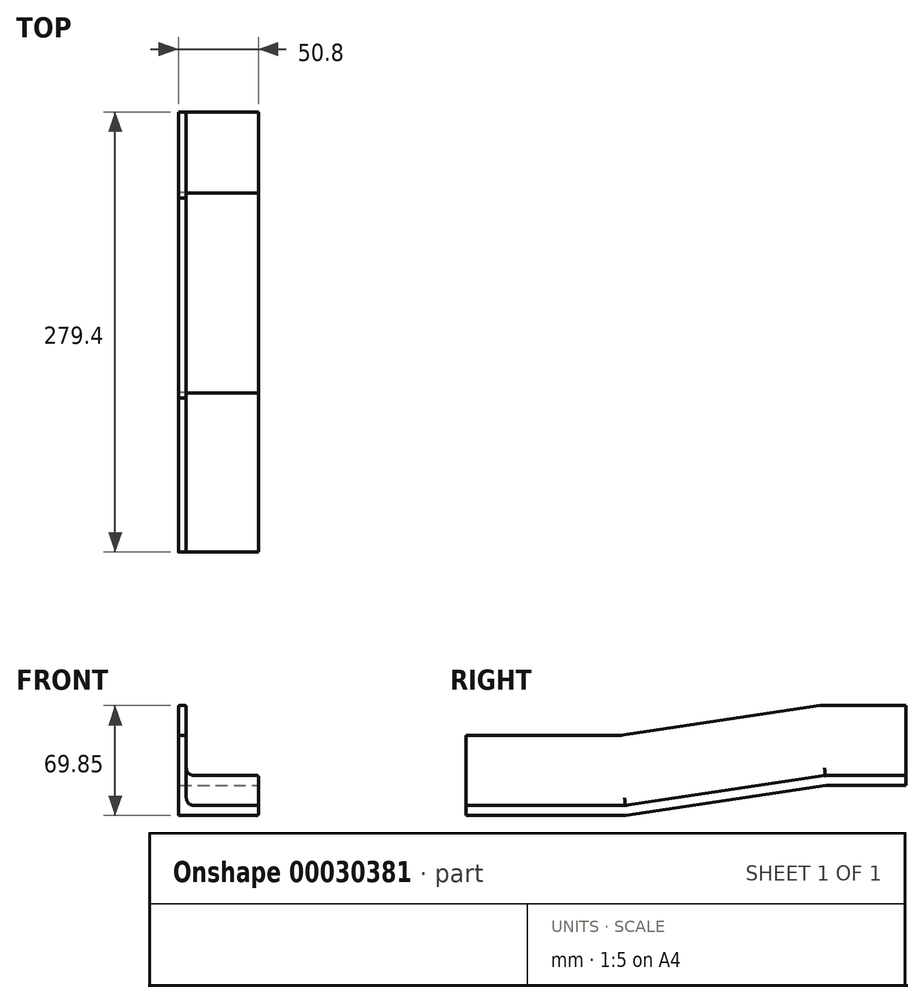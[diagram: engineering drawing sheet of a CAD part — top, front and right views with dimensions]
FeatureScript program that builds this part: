
annotation { "Feature Type Name" : "Feature", "Feature Type Description" : "" }
export const myFeature = defineFeature(function(context is Context, id is Id, definition is map)
    precondition{}
    {
        {
            var Q0;
            Q0=qCreatedBy(makeId("Front.planeOp"),FACE);
            var sketch = newSketch(context, id + "F0", { "sketchPlane" : qUnion([Q0])});
            skLineSegment(sketch, "E0", {"start": v(0, 50.01) * mm, "end": v(0, 0.79) * mm});
            skLineSegment(sketch, "E1", {"start": v(0.79, 0) * mm, "end": v(50.01, 0) * mm});
            skLineSegment(sketch, "E2", {"start": v(50.8, 0.79) * mm, "end": v(50.8, 5.56) * mm});
            skLineSegment(sketch, "E3", {"start": v(50.01, 6.35) * mm, "end": v(9.9, 6.35) * mm});
            skLineSegment(sketch, "E4", {"start": v(5.08, 11.18) * mm, "end": v(5.08, 50.01) * mm});
            skLineSegment(sketch, "E5", {"start": v(4.3, 50.8) * mm, "end": v(0.79, 50.8) * mm});
            skArc(sketch, "E6.filletArc", {"start": v(5.08, 11.18) * mm, "mid": v(6.5, 7.76) * mm, "end": v(9.9, 6.35) * mm});
            skPoint(sketch, "E7.visualSharp", {"position": v(0, 50.8) * mm});
            skArc(sketch, "E7.filletArc", {"start": v(0.79, 50.8) * mm, "mid": v(0.23, 50.57) * mm, "end": v(0, 50.01) * mm});
            skPoint(sketch, "E8.visualSharp", {"position": v(5.08, 50.8) * mm});
            skArc(sketch, "E8.filletArc", {"start": v(5.08, 50.01) * mm, "mid": v(4.85, 50.57) * mm, "end": v(4.3, 50.8) * mm});
            skPoint(sketch, "E9.visualSharp", {"position": v(50.8, 6.35) * mm});
            skArc(sketch, "E9.filletArc", {"start": v(50.8, 5.56) * mm, "mid": v(50.57, 6.12) * mm, "end": v(50.01, 6.35) * mm});
            skPoint(sketch, "E10.visualSharp", {"position": v(50.8, 0) * mm});
            skArc(sketch, "E10.filletArc", {"start": v(50.01, 0) * mm, "mid": v(50.57, 0.23) * mm, "end": v(50.8, 0.79) * mm});
            skPoint(sketch, "E11.visualSharp", {"position": v(0, 0) * mm});
            skArc(sketch, "E11.filletArc", {"start": v(0, 0.79) * mm, "mid": v(0.23, 0.23) * mm, "end": v(0.79, 0) * mm});
            skSolve(sketch);
        }
        {
            var Q0;
            Q0=qCreatedBy(makeId("Right.planeOp"),FACE);
            var sketch = newSketch(context, id + "F1", { "sketchPlane" : qUnion([Q0])});
            skLineSegment(sketch, "E12", {"start": v(0, 0) * mm, "end": v(101.6, 0) * mm});
            skLineSegment(sketch, "E13", {"start": v(101.6, 0) * mm, "end": v(228.6, 19.05) * mm});
            skLineSegment(sketch, "E14", {"start": v(228.6, 19.05) * mm, "end": v(279.4, 19.05) * mm});
            skSolve(sketch);
        }
        {
            var Q0;
            Q0=makeQuery(id+"F0.imprint","IMPRINT",FACE,{"disambiguationData":[TD([[makeQuery(id+"F0.imprint","IMPRINT",EDGE,{"derivedFrom":sQuery(id+"F0.wireOp",EDGE,"E0")}),1.0]])]});
            var Q1;
            Q1 = qConstructionFilter(qBodyType(qCreatedBy(id + "F1" ,EDGE), BodyType.WIRE), ConstructionObject.NO);
            sweep(context, id + "F2", {"profiles" : qUnion([Q0]), "path" : qUnion([Q1])});
        }
    });
